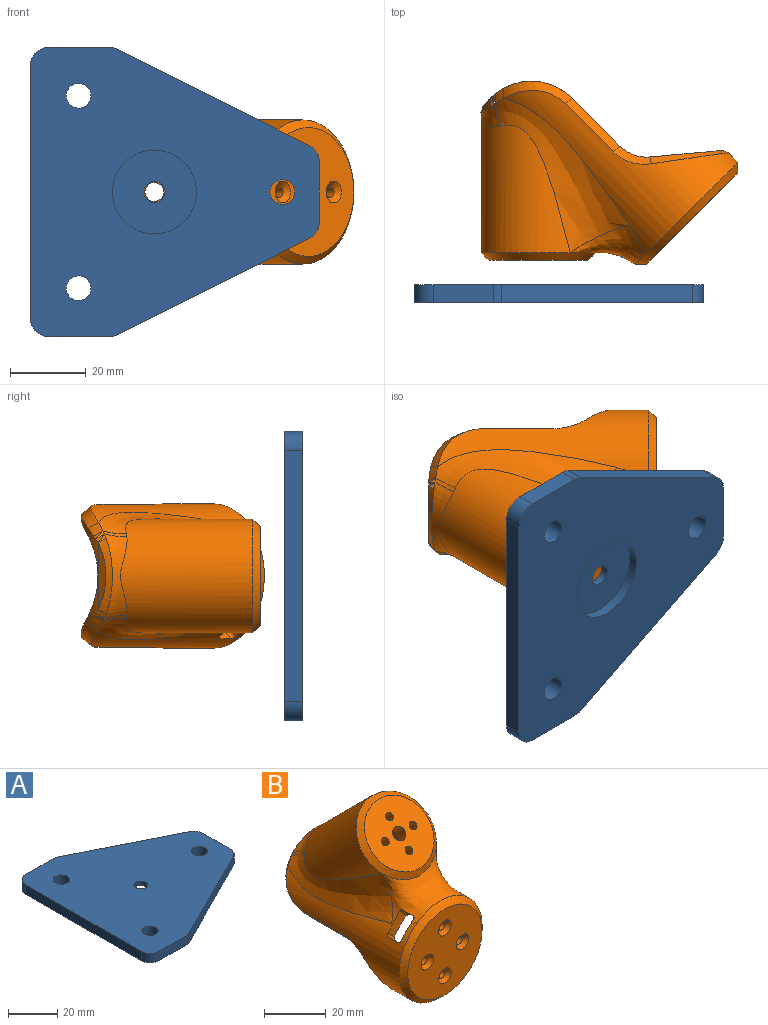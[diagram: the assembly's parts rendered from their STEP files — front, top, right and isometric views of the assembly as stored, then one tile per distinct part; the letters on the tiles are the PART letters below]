
ASSEMBLY  parts=2 mates=1
PART A: 20 faces, bbox 76.2x76.2x4.7 mm
  f0: plane 50.38x25.19mm, normal (0.45,0.89,0), area 262.5mm2, adj f1,f11,f12,f13
  f1: cylinder r=5mm len=4.66mm, axis (0,0,-1), area 10.8mm2, adj f0,f2,f12,f13
  f2: plane 15.82x4.66mm, normal (0,1,0), area 73.7mm2, adj f1,f3,f12,f13
  f3: cylinder r=5mm len=5mm, axis (0,0,-1), area 36.6mm2, adj f2,f4,f12,f13
  f4: plane 66.2x4.66mm, normal (-1,0,0), area 308.5mm2, adj f3,f5,f12,f13
  f5: cylinder r=5mm len=5mm, axis (0,0,-1), area 36.6mm2, adj f4,f6,f12,f13
  f6: plane 15.82x4.66mm, normal (0,-1,0), area 73.7mm2, adj f5,f7,f12,f13
  f7: cylinder r=5mm len=4.66mm, axis (0,0,-1), area 10.8mm2, adj f6,f8,f12,f13
  f8: plane 50.38x25.19mm, normal (0.45,-0.89,0), area 262.5mm2, adj f7,f9,f12,f13
  f9: cylinder r=5mm len=4.66mm, axis (0,0,-1), area 25.8mm2, adj f8,f10,f12,f13
  f10: plane 15.82x4.66mm, normal (1,0,0), area 73.7mm2, adj f9,f11,f12,f13
  f11: cylinder r=5mm len=4.66mm, axis (0,0,-1), area 25.8mm2, adj f0,f10,f12,f13
  f12: plane 76.2x76.2mm, normal (0,0,1), area 4200.1mm2, adj f0,f1,f2,f3,f4,f5,f6,f7
  f13: plane 76.2x76.2mm, normal (0,0,-1), area 3840.3mm2, adj f0,f1,f2,f3,f4,f5,f6,f7
  f14: cylinder r=3.25mm len=6.5mm, axis (0,0,-1), area 95.2mm2, adj f12,f13
  f15: cylinder r=3.25mm len=6.5mm, axis (0,0,-1), area 95.2mm2, adj f12,f13
  f16: cylinder r=3.25mm len=6.5mm, axis (0,0,-1), area 95.2mm2, adj f12,f13
  f17: cylinder r=11.05mm len=22.1mm, axis (0,0,-1), area 177.7mm2, adj f13,f18
  f18: plane 22.1x22.1mm, normal (0,0,-1), area 359.8mm2, adj f17,f19
  f19: cylinder r=2.75mm len=5.5mm, axis (0,0,-1), area 36.3mm2, adj f12,f18
PART B: 58 faces, bbox 38.3x61.3x64.9 mm
  f0: cylinder r=19mm len=55.49mm, axis (0,-1,0), area 1562.3mm2, adj f1,f6,f15,f35,f36,f38,f40,f42
  f1: bspline ~28.32x16.99mm, area 384.4mm2, adj f0,f6,f15,f24,f35,f36,f52,f53
  f2: plane 17.7x2.96mm, normal (0,1,0), area 35.1mm2, adj f21,f43
  f3: cylinder r=15mm len=1mm, axis (0,1,0), area 0.5mm2, adj f4,f6,f55
  f4: cylinder r=15mm len=56mm, axis (0,1,0), area 2520.8mm2, adj f3,f6,f16,f17,f18,f19,f20,f21
  f5: plane 34x34mm, normal (0,-1,0), area 804.1mm2, adj f8,f10,f12,f14,f15
  f6: plane 31.15x31.09mm, normal (0,1,0), area 710.9mm2, adj f0,f1,f3,f4,f7,f9,f11,f13
  f7: cylinder r=1.5mm len=3mm, axis (0,-1,0), area 24.7mm2, adj f6,f8
  f8: cone r=1.5mm half-angle=45deg, axis (0,-1,0), area 26.7mm2, adj f5,f7
  f9: cylinder r=1.5mm len=3mm, axis (0,-1,0), area 24.7mm2, adj f6,f10
  f10: cone r=1.5mm half-angle=45deg, axis (0,-1,0), area 26.7mm2, adj f5,f9
  f11: cylinder r=1.5mm len=3mm, axis (0,-1,0), area 24.7mm2, adj f6,f12
  f12: cone r=1.5mm half-angle=45deg, axis (0,-1,0), area 26.7mm2, adj f5,f11
  f13: cylinder r=1.5mm len=3mm, axis (0,-1,0), area 24.7mm2, adj f6,f14
  f14: cone r=1.5mm half-angle=45deg, axis (0,-1,0), area 26.7mm2, adj f5,f13
  f15: cone r=17mm half-angle=45deg, axis (0,1,0), area 319.9mm2, adj f0,f1,f5
  f16: plane 33.72x14.74mm, normal (0,0.77,-0.64), area 168.3mm2, adj f4,f19,f20,f44
  f17: plane 17.95x1.88mm, normal (0,0,-1), area 33.8mm2, adj f4,f20,f21,f40
  f18: plane 17.95x1.88mm, normal (0,0,-1), area 33.8mm2, adj f4,f19,f21,f48
  f19: cylinder r=10mm len=7.68mm, axis (-1,0,0), area 18.2mm2, adj f4,f16,f18,f46
  f20: cylinder r=10mm len=7.68mm, axis (-1,0,0), area 18.2mm2, adj f4,f16,f17,f42
  f21: cylinder r=15mm len=33.76mm, axis (-1,0,0), area 100.5mm2, adj f2,f4,f17,f18,f37,f38,f39,f41
  f22: cylinder r=15mm len=41.2mm, axis (0,0.71,-0.71), area 1812.5mm2, adj f24,f32,f33,f34,f35,f36
  f23: plane 26x18.38mm, normal (0,-0.71,0.71), area 484.9mm2, adj f24,f27,f28,f29,f30,f31
  f24: cone r=15mm half-angle=45deg, axis (0,0.71,-0.71), area 248.8mm2, adj f1,f22,f23
  f25: cylinder r=9.75mm len=38.59mm, axis (0,-0.71,0.71), area 1676.4mm2, adj f4,f26
  f26: plane 19.5x13.79mm, normal (0,0.71,-0.71), area 252.6mm2, adj f25,f27,f28,f29,f30,f31
  f27: cylinder r=1.45mm len=5.59mm, axis (0,-0.71,0.71), area 45.6mm2, adj f23,f26
  f28: cylinder r=2.5mm len=7.07mm, axis (0,-0.71,0.71), area 78.5mm2, adj f23,f26
  f29: cylinder r=1.45mm len=5.59mm, axis (0,-0.71,0.71), area 45.6mm2, adj f23,f26
  f30: cylinder r=1.45mm len=5.59mm, axis (0,-0.71,0.71), area 45.6mm2, adj f23,f26
  f31: cylinder r=1.45mm len=5.59mm, axis (0,-0.71,0.71), area 45.6mm2, adj f23,f26
  f32: bspline ~24.73x7.17mm, area 92mm2, adj f22,f33,f34,f41,f43,f45
  f33: bspline ~7.45x5.95mm, area 6.7mm2, adj f22,f32,f35,f39
  f34: bspline ~7.45x5.95mm, area 6.7mm2, adj f22,f32,f36,f47
  f35: bspline ~54.86x22.59mm, area 473.9mm2, adj f0,f1,f22,f33,f37
  f36: bspline ~53.68x21.8mm, area 474.4mm2, adj f0,f1,f22,f34,f49
  f37: bspline ~4.21x3.63mm, area 9.8mm2, adj f21,f35,f38,f39
  f38: bspline ~14.4x12.71mm, area 59.9mm2, adj f0,f21,f37,f40
  f39: bspline ~2.32x2.08mm, area 2.8mm2, adj f21,f33,f37,f41
  f40: plane 17.95x2.24mm, normal (-0.75,0,-0.66), area 53.6mm2, adj f0,f17,f38,f42
  f41: bspline ~2.43x2.24mm, area 3.4mm2, adj f21,f32,f39,f43
  f42: bspline ~9.21x5.83mm, area 28.1mm2, adj f0,f20,f40,f44
  f43: bspline ~19.95x4.53mm, area 40.7mm2, adj f2,f32,f41,f45
  f44: bspline ~37.66x16.45mm, area 123.1mm2, adj f0,f16,f42,f46
  f45: bspline ~2.43x2.24mm, area 3.4mm2, adj f21,f32,f43,f47
  f46: bspline ~9.21x5.83mm, area 28.1mm2, adj f0,f19,f44,f48
  f47: bspline ~2.32x2.08mm, area 2.8mm2, adj f21,f34,f45,f49
  f48: plane 17.95x2.24mm, normal (0.75,0,-0.66), area 53.6mm2, adj f0,f18,f46,f50
  f49: bspline ~4.21x3.63mm, area 9.8mm2, adj f21,f36,f47,f50
  f50: bspline ~14.4x12.71mm, area 59.9mm2, adj f0,f21,f48,f49
  f51: plane 4x2.96mm, normal (0.71,0,0.71), area 16.8mm2, adj f0,f4,f54,f57
  f52: plane 4.29x4.14mm, normal (-0.71,0,-0.71), area 19.9mm2, adj f1,f4,f55,f56
  f53: plane 9.31x8.57mm, normal (0,-1,0), area 33.9mm2, adj f0,f1,f4,f56,f57
  f54: cylinder r=1mm len=3.84mm, axis (-0.71,0,0.71), area 6.5mm2, adj f0,f4,f6,f51
  f55: cylinder r=1mm len=3.92mm, axis (0.71,0,-0.71), area 6.9mm2, adj f1,f3,f6,f52
  f56: cylinder r=1mm len=4.58mm, axis (0.71,0,-0.71), area 8.3mm2, adj f1,f4,f52,f53
  f57: cylinder r=1mm len=3.84mm, axis (-0.71,0,0.71), area 6.5mm2, adj f0,f4,f51,f53
PLACE A rot(axis=(-1,0,0),90deg) t=(-53.33,-151.11,51)mm
PLACE B rot(axis=(0.36,-0.86,0.36),98.4deg) t=(-12.8,-80.99,51)mm
MATE cylindrical A.f19 <-> B.f22  axis (0,-1,0) through (-53.33,-99.5,51)mm
